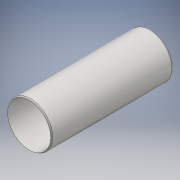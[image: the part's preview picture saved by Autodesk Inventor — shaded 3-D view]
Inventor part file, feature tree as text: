
AUTODESK INVENTOR PART (.ipt)
format: ipt  version: 2016 (Build 200138000, 138)  size: 119,296 bytes
history: native  units: mm
features: fillet x2, extrude x1, sketch x1
ambient origin geometry x8: Origin, YZ Plane, XZ Plane, XY Plane, X Axis, Y Axis, Z Axis, Center Point
bodies: Body1 (feature_tree)
feature tree (4):
  extrude  "Extrusion2"  Depth=2.0mm
  fillet  "Fillet1"  Radius=158.0mm
  fillet  "Fillet2"  Radius=2.0mm
  sketch  "Sketch2"  dims[d14=58.0mm d15=56.0mm d16=158.0mm d17=0.0mm d18=2.0mm d19=2.0mm]
